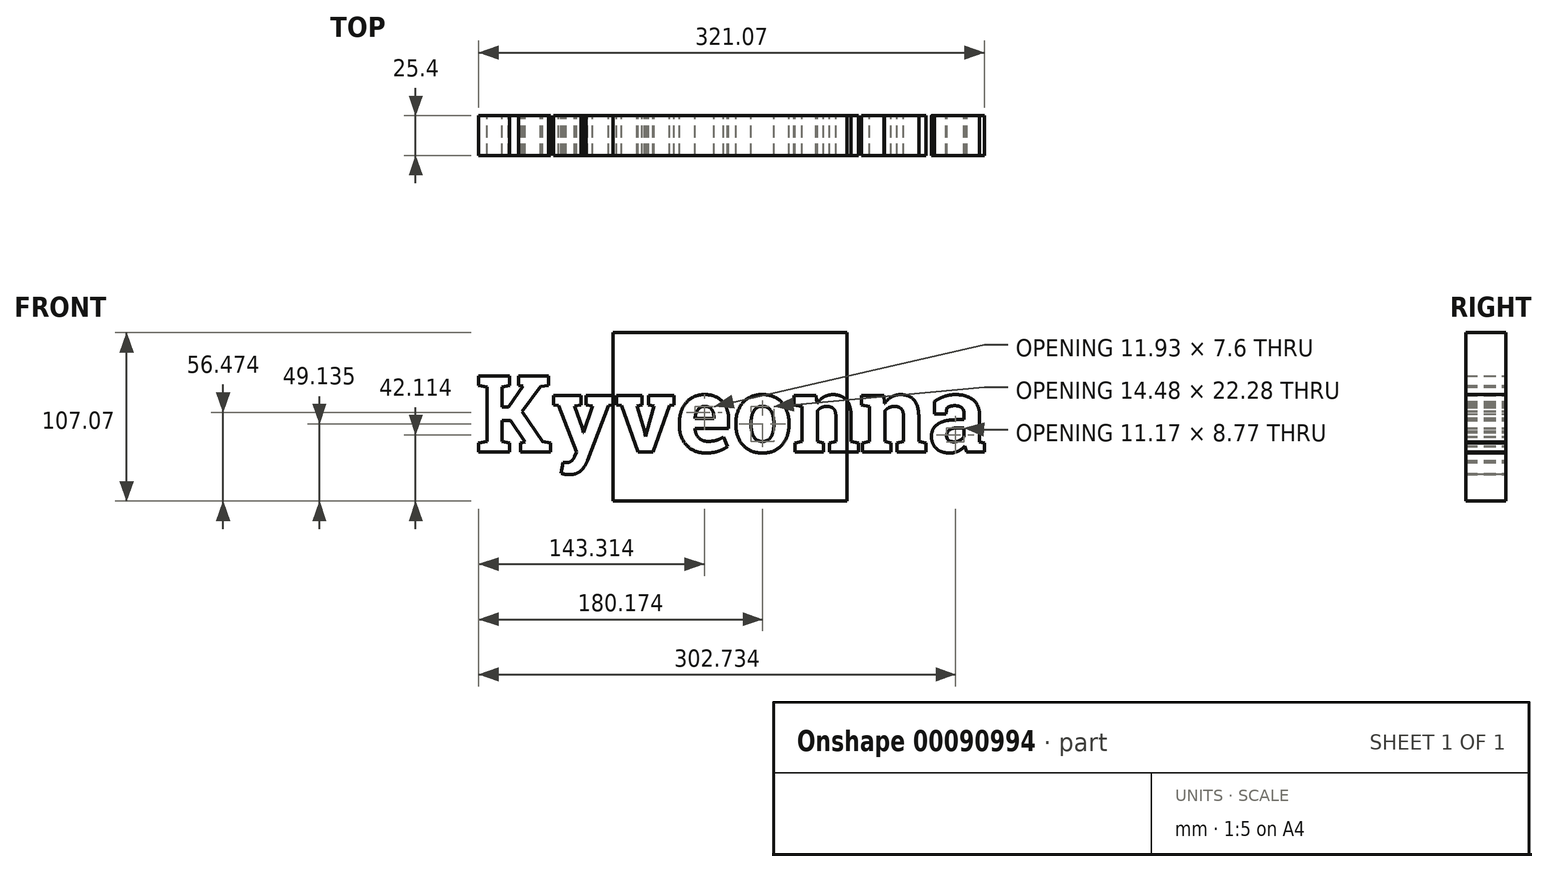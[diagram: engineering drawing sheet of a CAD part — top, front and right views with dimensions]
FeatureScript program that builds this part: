
annotation { "Feature Type Name" : "Feature", "Feature Type Description" : "" }
export const myFeature = defineFeature(function(context is Context, id is Id, definition is map)
    precondition{}
    {
        {
            var Q0;
            Q0=qCreatedBy(makeId("Front.planeOp"),FACE);
            var sketch = newSketch(context, id + "F0", { "sketchPlane" : qUnion([Q0])});
            skLineSegment(sketch, "E0.bottom", {"start": v(-74.27, 54) * mm, "end": v(74.27, 54) * mm});
            skLineSegment(sketch, "E0.top", {"start": v(-74.27, -53.07) * mm, "end": v(74.27, -53.07) * mm});
            skLineSegment(sketch, "E0.left", {"start": v(-74.27, 54) * mm, "end": v(-74.27, -53.07) * mm});
            skLineSegment(sketch, "E0.right", {"start": v(74.27, 54) * mm, "end": v(74.27, -53.07) * mm});
            skSolve(sketch);
        }
        {
            var Q0;
            Q0=makeQuery(id+"F0.imprint","IMPRINT",FACE,{"disambiguationData":[TD([[makeQuery(id+"F0.imprint","IMPRINT",EDGE,{"derivedFrom":sQuery(id+"F0.wireOp",EDGE,"E0.bottom")}),-1.0]])]});
            var sketch = newSketch(context, id + "F1", { "sketchPlane" : qUnion([Q0])});
            skSolve(sketch);
        }
        {
            var Q0;
            Q0=makeQuery(id+"F1.imprint","IMPRINT",FACE,{"disambiguationData":[TD([[makeQuery(id+"F1.imprint","IMPRINT",EDGE,{"derivedFrom":makeQuery(id+"F0.imprint","IMPRINT",EDGE,{"derivedFrom":sQuery(id+"F0.wireOp",EDGE,"E0.bottom")})}),-1.0]])]});
            var sketch = newSketch(context, id + "F2", { "sketchPlane" : qUnion([Q0])});
            skText(sketch, "E1", { "text": "Kyveonna", "fontName": "RobotoSlab-Bold.ttf"});
            const initialGuessF2  = {"E1": [-0.16139, -0.02178, 1, 0, 0.04873]};
            skSetInitialGuess(sketch, initialGuessF2);
            skSolve(sketch);
        }
        {
            var Q0;
            Q0=makeQuery(id+"F1.imprint","IMPRINT",FACE,{"disambiguationData":[TD([[makeQuery(id+"F1.imprint","IMPRINT",EDGE,{"derivedFrom":makeQuery(id+"F0.imprint","IMPRINT",EDGE,{"derivedFrom":sQuery(id+"F0.wireOp",EDGE,"E0.bottom")})}),-1.0]])]});
            var Q1;
            Q1 = qSketchRegion(id + "F2", true);
            extrude(context, id + "F3", {"entities" : qUnion([Q0, Q1]), "depth" : 25.4 * mm});
        }
    });
